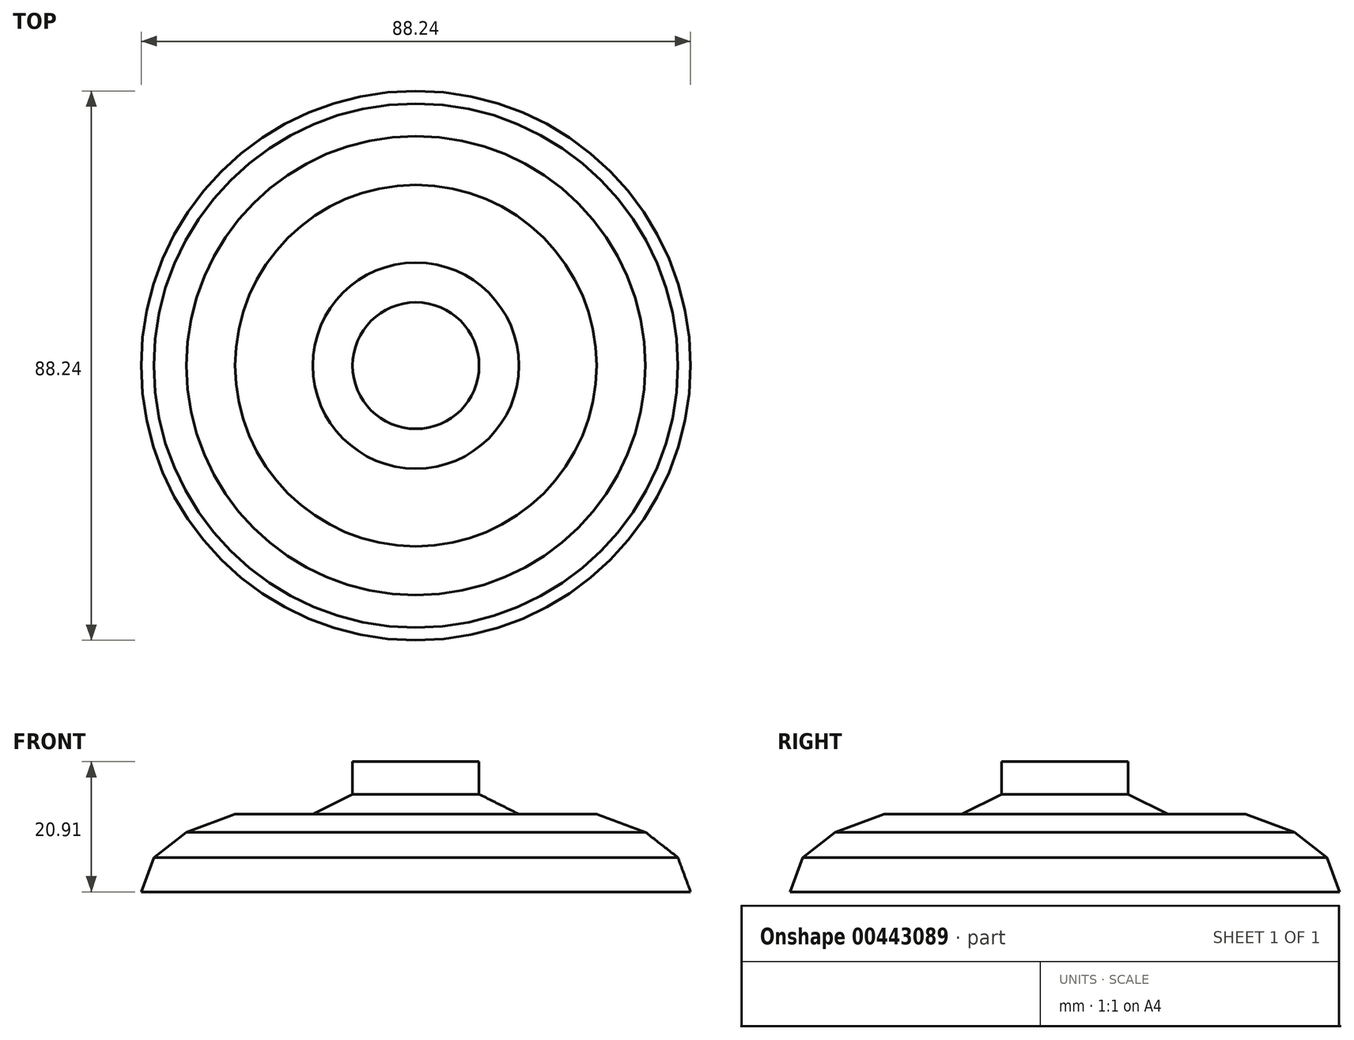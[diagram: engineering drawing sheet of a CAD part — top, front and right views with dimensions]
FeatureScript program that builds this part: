
annotation { "Feature Type Name" : "Feature", "Feature Type Description" : "" }
export const myFeature = defineFeature(function(context is Context, id is Id, definition is map)
    precondition{}
    {
        {
            var Q0;
            Q0=qCreatedBy(makeId("Front.planeOp"),FACE);
            var sketch = newSketch(context, id + "F0", { "sketchPlane" : qUnion([Q0])});
            skLineSegment(sketch, "E0", {"start": v(0, -40.79) * mm, "end": v(-44.12, -40.79) * mm});
            skLineSegment(sketch, "E1", {"start": v(-44.12, -40.79) * mm, "end": v(-42.1, -35.27) * mm});
            skLineSegment(sketch, "E2", {"start": v(-42.1, -35.27) * mm, "end": v(-36.87, -31.2) * mm});
            skLineSegment(sketch, "E3", {"start": v(-36.87, -31.2) * mm, "end": v(-29.03, -28.3) * mm});
            skLineSegment(sketch, "E4", {"start": v(-29.03, -28.3) * mm, "end": v(-16.55, -28.3) * mm});
            skLineSegment(sketch, "E5", {"start": v(-16.55, -28.3) * mm, "end": v(-10.16, -25.1) * mm});
            skLineSegment(sketch, "E6", {"start": v(-10.16, -25.1) * mm, "end": v(-10.16, -19.88) * mm});
            skLineSegment(sketch, "E7", {"start": v(-10.16, -19.88) * mm, "end": v(0, -19.88) * mm});
            skLineSegment(sketch, "E8", {"start": v(0, -19.88) * mm, "end": v(0, -40.79) * mm});
            skSolve(sketch);
        }
        {
            var Q0;
            Q0=makeQuery(id+"F0.imprint","IMPRINT",FACE,{"disambiguationData":[TD([[makeQuery(id+"F0.imprint","IMPRINT",EDGE,{"derivedFrom":sQuery(id+"F0.wireOp",EDGE,"E0")}),-1.0]])]});
            var Q1;
            Q1=sQuery(id+"F0.wireOp",EDGE,"E8");
            revolve(context, id + "F1", {"entities" : qUnion([Q0]), "axis" : qUnion([Q1]), "revolveType" : RevolveType.FULL});
        }
    });
